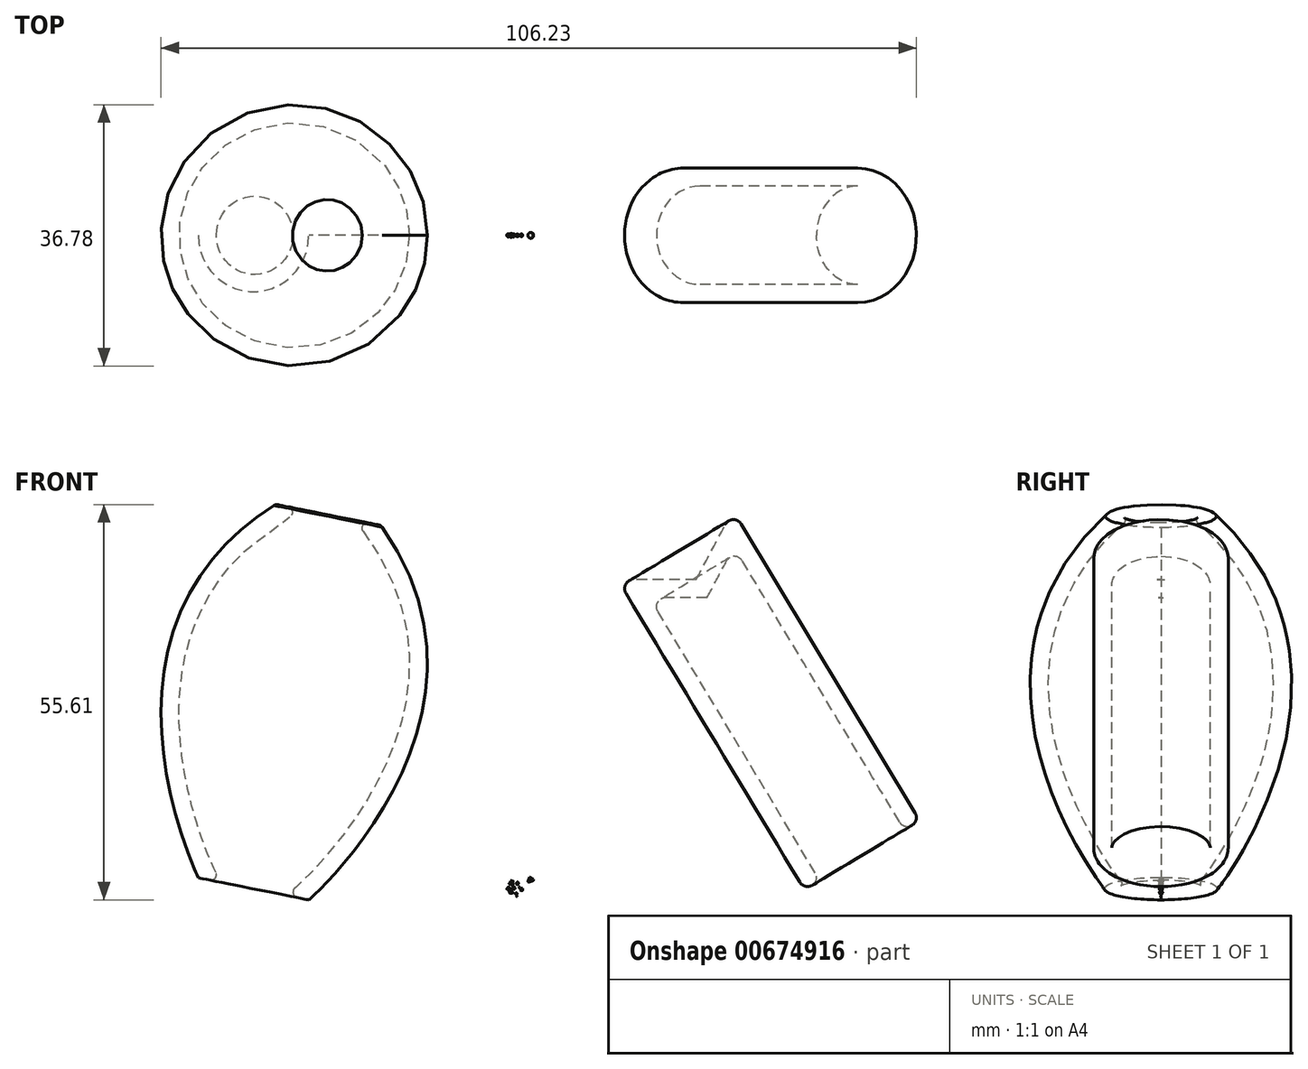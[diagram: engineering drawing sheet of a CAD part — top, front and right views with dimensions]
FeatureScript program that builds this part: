
annotation { "Feature Type Name" : "Feature", "Feature Type Description" : "" }
export const myFeature = defineFeature(function(context is Context, id is Id, definition is map)
    precondition{}
    {
        {
            var Q0;
            Q0=qCreatedBy(makeId("Front.planeOp"),FACE);
            var sketch = newSketch(context, id + "F0", { "sketchPlane" : qUnion([Q0])});
            skLineSegment(sketch, "E0", {"start": v(6.36, 22.21) * mm, "end": v(29.77, -16.68) * mm});
            skLineSegment(sketch, "E1", {"start": v(11.52, 31.99) * mm, "end": v(37.79, -11.65) * mm});
            skLineSegment(sketch, "E2", {"start": v(11.52, 31.99) * mm, "end": v(6.36, 22.21) * mm});
            skLineSegment(sketch, "E3", {"start": v(37.79, -11.65) * mm, "end": v(29.77, -16.68) * mm});
            skSolve(sketch);
        }
        {
            var Q0;
            Q0 = qSketchRegion(id + "F0", true);
            var Q1;
            Q1=sQuery(id+"F0.wireOp",EDGE,"E0");
            revolve(context, id + "F1", {"entities" : qUnion([Q0]), "axis" : qUnion([Q1]), "revolveType" : RevolveType.FULL});
        }
        {
            var Q0;
            Q0=makeQuery(id+"F1.opRevolve","SWEPT_FACE",FACE,{"disambiguationData":[OSD([sQuery(id+"F0.wireOp",EDGE,"E3")])]});
            shell(context, id + "F2", {"entities" : qUnion([Q0]), "thickness" : 2.54 * mm});
        }
        {
            var Q0;
            Q0=makeQuery(id+"F2.opShell","OFFSET_EDGE",EDGE,{"disambiguationData":[OSD([sQuery(id+"F0.wireOp",EDGE,"E1"),sQuery(id+"F0.wireOp",EDGE,"E3")])]});
            var Q1;
            Q1=makeQuery(id+"F1.opRevolve","SWEPT_EDGE",EDGE,{"disambiguationData":[OSD([sQuery(id+"F0.wireOp",EDGE,"E1"),sQuery(id+"F0.wireOp",EDGE,"E3")])]});
            var Q2;
            Q2=makeQuery(id+"F2.opShell","OFFSET_EDGE",EDGE,{"disambiguationData":[OSD([sQuery(id+"F0.wireOp",EDGE,"E1"),sQuery(id+"F0.wireOp",EDGE,"E2")])]});
            var Q3;
            Q3=makeQuery(id+"F1.opRevolve","SWEPT_EDGE",EDGE,{"disambiguationData":[OSD([sQuery(id+"F0.wireOp",EDGE,"E1"),sQuery(id+"F0.wireOp",EDGE,"E2")])]});
            fillet(context, id + "F3", {"entities" : qUnion([Q0, Q1, Q2, Q3]), "radius" : 1.27 * mm, "tangentPropagation" : true, "allowEdgeOverflow" : false});
        }
        {
            var Q0;
            Q0=qCreatedBy(makeId("Front.planeOp"),FACE);
            var sketch = newSketch(context, id + "F4", { "sketchPlane" : qUnion([Q0])});
            skLineSegment(sketch, "E4", {"start": v(-45.37, 31.3) * mm, "end": v(-55.87, -21.25) * mm});
            skFitSpline(sketch, "E5", {"points": [v(-37.95, 29.86) * mm, v(-48.12, -22.83) * mm, v(-48.2, -22.58) * mm], "startDerivative": vector(60.75, -85.59) * mm, "endDerivative": vector(-4.15, 11.51) * mm});
            skLineSegment(sketch, "E6", {"start": v(-37.95, 29.86) * mm, "end": v(-45.37, 31.3) * mm});
            skLineSegment(sketch, "E7", {"start": v(-48.12, -22.83) * mm, "end": v(-55.87, -21.25) * mm});
            skSolve(sketch);
        }
        {
            var Q0;
            {var subQ5=sQuery(id+"F4.wireOp",EDGE,"E4");Q0=makeQuery(id+"F4.imprint","IMPRINT",FACE,{"disambiguationData":[TD([[makeQuery(id+"F4.imprint","IMPRINT",EDGE,{"derivedFrom":subQ5}),1.0]])]});}
            var Q1;
            Q1=sQuery(id+"F4.wireOp",EDGE,"E4");
            revolve(context, id + "F5", {"entities" : qUnion([Q0]), "axis" : qUnion([Q1]), "revolveType" : RevolveType.FULL});
        }
        {
            var Q0;
            Q0=makeQuery(id+"F5.opRevolve","SWEPT_FACE",FACE,{"disambiguationData":[OSD([sQuery(id+"F4.wireOp",EDGE,"E7")])]});
            var Q1;
            Q1=makeQuery(id+"F5.opRevolve","SWEPT_FACE",FACE,{"disambiguationData":[OSD([sQuery(id+"F4.wireOp",EDGE,"E6")])]});
            shell(context, id + "F6", {"entities" : qUnion([Q0, Q1]), "thickness" : 2.54 * mm});
        }
        {
            var Q0;
            Q0=makeQuery(id+"F5.opRevolve","SWEPT_EDGE",EDGE,{"disambiguationData":[OSD([sQuery(id+"F4.wireOp",EDGE,"E5"),sQuery(id+"F4.wireOp",EDGE,"E6")])]});
            var Q1;
            Q1=makeQuery(id+"F6.opShell","OFFSET_EDGE",EDGE,{"disambiguationData":[OSD([sQuery(id+"F4.wireOp",EDGE,"E5"),sQuery(id+"F4.wireOp",EDGE,"E6")])]});
            var Q2;
            Q2=makeQuery(id+"F6.opShell","OFFSET_EDGE",EDGE,{"disambiguationData":[OSD([sQuery(id+"F4.wireOp",EDGE,"E5"),sQuery(id+"F4.wireOp",EDGE,"E7")])]});
            fillet(context, id + "F7", {"entities" : qUnion([Q0, Q1, Q2]), "radius" : 0.76 * mm, "tangentPropagation" : true, "allowEdgeOverflow" : false});
        }
        {
            var Q0;
            Q0=qCreatedBy(makeId("Front.planeOp"),FACE);
            var sketch = newSketch(context, id + "F8", { "sketchPlane" : qUnion([Q0])});
            skLineSegment(sketch, "E8", {"start": v(-19.66, -21.6) * mm, "end": v(-19.66, -21.9) * mm});
            skFitSpline(sketch, "E9", {"points": [v(-19.66, -21.6) * mm, v(-19.66, -21.9) * mm], "startDerivative": vector(0, -0.1) * mm, "endDerivative": vector(-1.78, -0.17) * mm});
            skSolve(sketch);
        }
        {
            var Q0;
            Q0 = qSketchRegion(id + "F8", true);
            var Q1;
            Q1=sQuery(id+"F8.wireOp",EDGE,"E8");
            revolve(context, id + "F9", {"entities" : qUnion([Q0]), "axis" : qUnion([Q1]), "revolveType" : RevolveType.FULL});
        }
        {
            var Q0;
            Q0=qCreatedBy(makeId("Front.planeOp"),FACE);
            var sketch = newSketch(context, id + "F10", { "sketchPlane" : qUnion([Q0])});
            skLineSegment(sketch, "E10", {"start": v(-18.82, -21.9) * mm, "end": v(-19.05, -22.03) * mm});
            skLineSegment(sketch, "E11", {"start": v(-18.82, -21.9) * mm, "end": v(-18.82, -22.02) * mm});
            skLineSegment(sketch, "E12", {"start": v(-18.82, -22.02) * mm, "end": v(-18.88, -22.1) * mm});
            skLineSegment(sketch, "E13", {"start": v(-18.88, -22.1) * mm, "end": v(-18.99, -22.1) * mm});
            skLineSegment(sketch, "E14", {"start": v(-18.99, -22.1) * mm, "end": v(-19.05, -22.03) * mm});
            skSolve(sketch);
        }
        {
            var Q0;
            Q0 = qSketchRegion(id + "F10", true);
            var Q1;
            Q1=sQuery(id+"F10.wireOp",EDGE,"E10");
            revolve(context, id + "F11", {"entities" : qUnion([Q0]), "axis" : qUnion([Q1]), "revolveType" : RevolveType.FULL});
        }
        {
            var Q0;
            Q0=qCreatedBy(makeId("Front.planeOp"),FACE);
            var sketch = newSketch(context, id + "F12", { "sketchPlane" : qUnion([Q0])});
            skLineSegment(sketch, "E15", {"start": v(-19.9, -21.11) * mm, "end": v(-20.2, -21.41) * mm});
            skLineSegment(sketch, "E16", {"start": v(-20.2, -21.41) * mm, "end": v(-19.95, -21.48) * mm});
            skLineSegment(sketch, "E17", {"start": v(-19.95, -21.48) * mm, "end": v(-20.02, -21.35) * mm});
            skLineSegment(sketch, "E18", {"start": v(-20.02, -21.35) * mm, "end": v(-19.87, -21.41) * mm});
            skLineSegment(sketch, "E19", {"start": v(-19.87, -21.41) * mm, "end": v(-19.87, -21.25) * mm});
            skLineSegment(sketch, "E20", {"start": v(-19.87, -21.25) * mm, "end": v(-19.76, -21.25) * mm});
            skLineSegment(sketch, "E21", {"start": v(-19.76, -21.25) * mm, "end": v(-19.9, -21.11) * mm});
            skLineSegment(sketch, "E22", {"start": v(-18.62, -21.35) * mm, "end": v(-18.62, -20.96) * mm});
            skFitSpline(sketch, "E23", {"points": [v(-18.62, -20.96) * mm, v(-18.62, -21.35) * mm], "startDerivative": vector(1.15, -0.04) * mm, "endDerivative": vector(1.17, 0) * mm});
            skSolve(sketch);
        }
        {
            var Q0;
            Q0=makeQuery(id+"F12.imprint","IMPRINT",FACE,{"disambiguationData":[TD([[makeQuery(id+"F12.imprint","IMPRINT",EDGE,{"derivedFrom":sQuery(id+"F12.wireOp",EDGE,"E15")}),1.0]])]});
            var Q1;
            Q1=sQuery(id+"F12.wireOp",EDGE,"E15");
            revolve(context, id + "F13", {"entities" : qUnion([Q0]), "axis" : qUnion([Q1]), "revolveType" : RevolveType.FULL});
        }
        {
            var Q0;
            {var subQ0=sQuery(id+"F12.wireOp",EDGE,"E23");var subQ1=sQuery(id+"F12.wireOp",EDGE,"E22");var subQ2=makeQuery(id+"F12.imprint","INTERSECT",VERTEX,{"disambiguationData":[OD(1.0)],"derivedFrom":[subQ1,subQ0]});Q0=makeQuery(id+"F12.imprint","IMPRINT",FACE,{"disambiguationData":[TD([[makeQuery(id+"F12.imprint","IMPRINT",EDGE,{"disambiguationData":[TD([[subQ2,1.0]])],"derivedFrom":subQ1}),-1.0]])]});}
            var Q1;
            {var subQ0=sQuery(id+"F12.wireOp",EDGE,"E23");var subQ1=sQuery(id+"F12.wireOp",EDGE,"E22");var subQ2=makeQuery(id+"F12.imprint","INTERSECT",VERTEX,{"disambiguationData":[OD(0.0)],"derivedFrom":[subQ1,subQ0]});Q1=makeQuery(id+"F12.imprint","IMPRINT",FACE,{"disambiguationData":[TD([[makeQuery(id+"F12.imprint","IMPRINT",EDGE,{"disambiguationData":[TD([[subQ2,-1.0]])],"derivedFrom":subQ1}),1.0]])]});}
            var Q2;
            Q2=sQuery(id+"F12.wireOp",EDGE,"E22");
            revolve(context, id + "F14", {"entities" : qUnion([Q0, Q1]), "axis" : qUnion([Q2]), "revolveType" : RevolveType.FULL});
        }
        {
            var Q0;
            Q0=qCreatedBy(makeId("Front.planeOp"),FACE);
            var sketch = newSketch(context, id + "F15", { "sketchPlane" : qUnion([Q0])});
            skLineSegment(sketch, "E24", {"start": v(-18.86, -22.29) * mm, "end": v(-18.86, -22.37) * mm});
            skLineSegment(sketch, "E25", {"start": v(-18.86, -22.29) * mm, "end": v(-18.8, -22.29) * mm});
            skFitSpline(sketch, "E26", {"points": [v(-18.8, -22.29) * mm, v(-18.8, -22.37) * mm], "startDerivative": vector(-0.2, -0.12) * mm, "endDerivative": vector(0.13, -0.08) * mm});
            skLineSegment(sketch, "E27", {"start": v(-18.8, -22.37) * mm, "end": v(-18.86, -22.37) * mm});
            skLineSegment(sketch, "E28", {"start": v(-18.5, -22.38) * mm, "end": v(-18.61, -22.5) * mm});
            skFitSpline(sketch, "E29", {"points": [v(-18.5, -22.38) * mm, v(-18.61, -22.5) * mm], "startDerivative": vector(0.5, 0.2) * mm, "endDerivative": vector(0, 0.54) * mm});
            skSolve(sketch);
        }
        {
            var Q0;
            Q0=makeQuery(id+"F15.imprint","IMPRINT",FACE,{"disambiguationData":[TD([[makeQuery(id+"F15.imprint","IMPRINT",EDGE,{"derivedFrom":sQuery(id+"F15.wireOp",EDGE,"E24")}),1.0]])]});
            var Q1;
            Q1=sQuery(id+"F15.wireOp",EDGE,"E24");
            revolve(context, id + "F16", {"entities" : qUnion([Q0]), "axis" : qUnion([Q1]), "revolveType" : RevolveType.FULL});
        }
        {
            var Q0;
            Q0=makeQuery(id+"F11.opRevolve","SWEPT_EDGE",EDGE,{"disambiguationData":[OSD([sQuery(id+"F10.wireOp",EDGE,"E11"),sQuery(id+"F10.wireOp",EDGE,"E12")])]});
            var Q1;
            Q1=makeQuery(id+"F11.opRevolve","SWEPT_EDGE",EDGE,{"disambiguationData":[OSD([sQuery(id+"F10.wireOp",EDGE,"E12"),sQuery(id+"F10.wireOp",EDGE,"E13")])]});
            fillet(context, id + "F17", {"entities" : qUnion([Q0, Q1]), "radius" : 0.09 * mm, "tangentPropagation" : true, "allowEdgeOverflow" : false});
        }
        {
            var Q0;
            Q0=qCreatedBy(makeId("Front.planeOp"),FACE);
            var sketch = newSketch(context, id + "F18", { "sketchPlane" : qUnion([Q0])});
            skLineSegment(sketch, "E30", {"start": v(-19.54, -20.2) * mm, "end": v(-19.33, -20.23) * mm});
            skLineSegment(sketch, "E31", {"start": v(-19.33, -20.23) * mm, "end": v(-19.49, -20.43) * mm});
            skLineSegment(sketch, "E32", {"start": v(-19.54, -20.2) * mm, "end": v(-19.65, -20.58) * mm});
            skFitSpline(sketch, "E33", {"points": [v(-19.49, -20.43) * mm, v(-19.65, -20.58) * mm], "startDerivative": vector(0.76, -0.9) * mm, "endDerivative": vector(-0.4, 0.8) * mm});
            skSolve(sketch);
        }
        {
            var Q0;
            Q0 = qSketchRegion(id + "F18", true);
            var Q1;
            Q1=sQuery(id+"F18.wireOp",EDGE,"E32");
            revolve(context, id + "F19", {"entities" : qUnion([Q0]), "axis" : qUnion([Q1]), "revolveType" : RevolveType.FULL});
        }
        {
            var Q0;
            Q0=qCreatedBy(makeId("Front.planeOp"),FACE);
            var sketch = newSketch(context, id + "F20", { "sketchPlane" : qUnion([Q0])});
            skLineSegment(sketch, "E34", {"start": v(-18.8, -20.63) * mm, "end": v(-18.74, -20.38) * mm});
            skFitSpline(sketch, "E35", {"points": [v(-18.8, -20.63) * mm, v(-18.74, -20.38) * mm], "startDerivative": vector(0.41, -0.64) * mm, "endDerivative": vector(-0.46, -0.53) * mm});
            skFitSpline(sketch, "E36", {"points": [v(-18.8, -20.63) * mm, v(-18.74, -20.38) * mm], "startDerivative": vector(0.79, 0.3) * mm, "endDerivative": vector(-0.63, 0.47) * mm});
            skSolve(sketch);
        }
        {
            var Q0;
            Q0 = qSketchRegion(id + "F20", true);
            var Q1;
            Q1=sQuery(id+"F20.wireOp",EDGE,"E34");
            revolve(context, id + "F21", {"entities" : qUnion([Q0]), "axis" : qUnion([Q1]), "revolveType" : RevolveType.FULL});
        }
        {
            var Q0;
            {var subQ0=sQuery(id+"F20.wireOp",EDGE,"E36");var subQ1=sQuery(id+"F20.wireOp",EDGE,"E35");Q0=makeQuery(id+"F21.opRevolve","SWEPT_EDGE",EDGE,{"disambiguationData":[OSD([subQ1,subQ0]),TDD([makeQuery(id+"F20.imprint","INTERSECT",VERTEX,{"disambiguationData":[OD(0.0)],"derivedFrom":[subQ1,subQ0]})])]});}
            var Q1;
            {var subQ0=sQuery(id+"F20.wireOp",EDGE,"E36");var subQ1=sQuery(id+"F20.wireOp",EDGE,"E35");Q1=makeQuery(id+"F21.opRevolve","SWEPT_EDGE",EDGE,{"disambiguationData":[OSD([subQ1,subQ0]),TDD([makeQuery(id+"F20.imprint","INTERSECT",VERTEX,{"disambiguationData":[OD(1.0)],"derivedFrom":[subQ1,subQ0]})])]});}
            fillet(context, id + "F22", {"entities" : qUnion([Q0, Q1]), "radius" : 0.05 * mm, "tangentPropagation" : true, "allowEdgeOverflow" : false});
        }
        {
            var Q0;
            Q0=qCreatedBy(makeId("Front.planeOp"),FACE);
            var sketch = newSketch(context, id + "F23", { "sketchPlane" : qUnion([Q0])});
            skLineSegment(sketch, "E37", {"start": v(-17.07, -19.64) * mm, "end": v(-16.53, -19.95) * mm});
            skFitSpline(sketch, "E38", {"points": [v(-16.53, -19.95) * mm, v(-16.85, -20.28) * mm], "startDerivative": vector(0.51, -0.92) * mm, "endDerivative": vector(0.08, -0.62) * mm});
            skLineSegment(sketch, "E39", {"start": v(-17.07, -19.64) * mm, "end": v(-16.85, -20.28) * mm});
            skLineSegment(sketch, "E40", {"start": v(-18.2, -21.22) * mm, "end": v(-18.2, -21.54) * mm});
            skLineSegment(sketch, "E41", {"start": v(-18.2, -21.22) * mm, "end": v(-18.02, -21.22) * mm});
            skLineSegment(sketch, "E42", {"start": v(-18.02, -21.22) * mm, "end": v(-18.09, -21.37) * mm});
            skLineSegment(sketch, "E43", {"start": v(-18.09, -21.37) * mm, "end": v(-18.02, -21.47) * mm});
            skLineSegment(sketch, "E44", {"start": v(-18.02, -21.47) * mm, "end": v(-18.09, -21.52) * mm});
            skLineSegment(sketch, "E45", {"start": v(-18.09, -21.52) * mm, "end": v(-18.2, -21.54) * mm});
            skLineSegment(sketch, "E46", {"start": v(-19.32, -20.95) * mm, "end": v(-19.32, -21.22) * mm});
            skFitSpline(sketch, "E47", {"points": [v(-19.32, -20.95) * mm, v(-19.32, -21.22) * mm], "startDerivative": vector(1.09, -0.29) * mm, "endDerivative": vector(-0.62, 1.07) * mm});
            skSolve(sketch);
        }
        {
            var Q0;
            Q0=makeQuery(id+"F23.imprint","IMPRINT",FACE,{"disambiguationData":[TD([[makeQuery(id+"F23.imprint","IMPRINT",EDGE,{"derivedFrom":sQuery(id+"F23.wireOp",EDGE,"E46")}),1.0]])]});
            var Q1;
            Q1=sQuery(id+"F23.wireOp",EDGE,"E46");
            revolve(context, id + "F24", {"entities" : qUnion([Q0]), "axis" : qUnion([Q1]), "revolveType" : RevolveType.FULL});
        }
        {
            var Q0;
            Q0=makeQuery(id+"F23.imprint","IMPRINT",FACE,{"disambiguationData":[TD([[makeQuery(id+"F23.imprint","IMPRINT",EDGE,{"derivedFrom":sQuery(id+"F23.wireOp",EDGE,"E40")}),1.0]])]});
            var Q1;
            Q1=sQuery(id+"F23.wireOp",EDGE,"E40");
            revolve(context, id + "F25", {"entities" : qUnion([Q0]), "axis" : qUnion([Q1]), "revolveType" : RevolveType.FULL});
        }
        {
            var Q0;
            Q0=makeQuery(id+"F23.imprint","IMPRINT",FACE,{"disambiguationData":[TD([[makeQuery(id+"F23.imprint","IMPRINT",EDGE,{"derivedFrom":sQuery(id+"F23.wireOp",EDGE,"E37")}),-1.0]])]});
            var Q1;
            Q1=sQuery(id+"F23.wireOp",EDGE,"E39");
            revolve(context, id + "F26", {"entities" : qUnion([Q0]), "axis" : qUnion([Q1]), "revolveType" : RevolveType.FULL});
        }
    });
